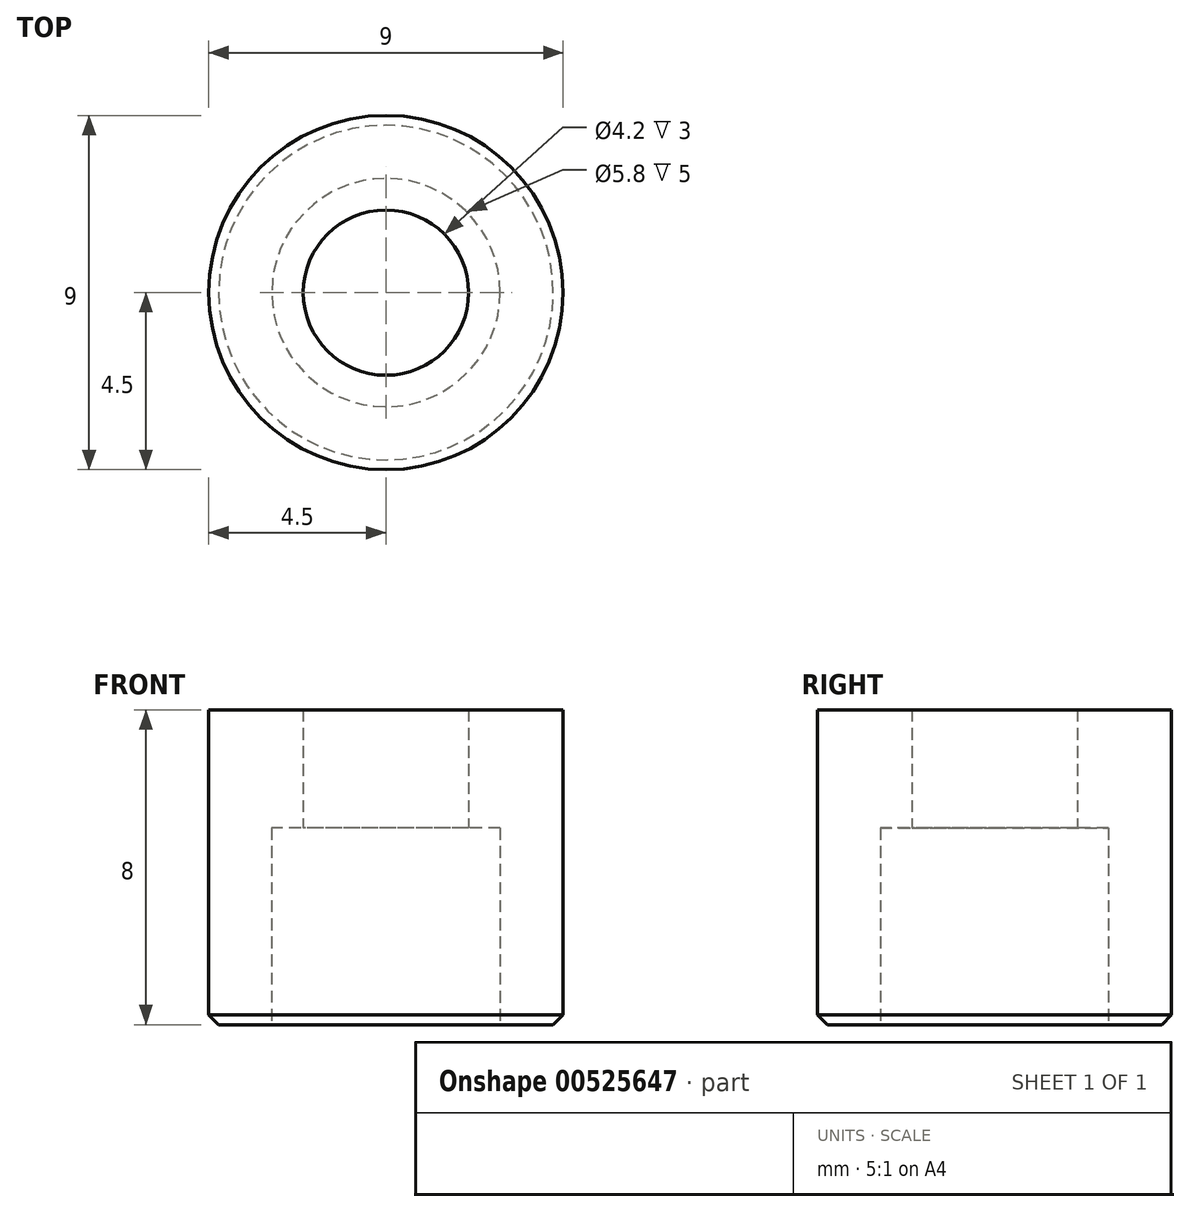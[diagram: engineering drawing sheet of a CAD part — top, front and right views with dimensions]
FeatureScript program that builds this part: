
annotation { "Feature Type Name" : "Feature", "Feature Type Description" : "" }
export const myFeature = defineFeature(function(context is Context, id is Id, definition is map)
    precondition{}
    {
        {
            var Q0;
            Q0=qCreatedBy(makeId("Top.planeOp"),FACE);
            var sketch = newSketch(context, id + "F0", { "sketchPlane" : qUnion([Q0])});
            skCircle(sketch, "E0", {"center": v(0, 0) * mm, "radius": 4.5 * mm});
            skCircle(sketch, "E1", {"center": v(0, 0) * mm, "radius": 2.9 * mm});
            skCircle(sketch, "E2", {"center": v(0, 0) * mm, "radius": 2.1 * mm});
            skSolve(sketch);
        }
        {
            var Q0;
            Q0=makeQuery(id+"F0.imprint","IMPRINT",FACE,{"disambiguationData":[TD([[makeQuery(id+"F0.imprint","IMPRINT",EDGE,{"derivedFrom":sQuery(id+"F0.wireOp",EDGE,"E2")}),1.0]])]});
            var Q1;
            Q1=makeQuery(id+"F0.imprint","IMPRINT",FACE,{"disambiguationData":[TD([[makeQuery(id+"F0.imprint","IMPRINT",EDGE,{"derivedFrom":sQuery(id+"F0.wireOp",EDGE,"E1")}),1.0]])]});
            var Q2;
            Q2=makeQuery(id+"F0.imprint","IMPRINT",FACE,{"disambiguationData":[TD([[makeQuery(id+"F0.imprint","IMPRINT",EDGE,{"derivedFrom":sQuery(id+"F0.wireOp",EDGE,"E0")}),1.0]])]});
            extrude(context, id + "F1", {"entities" : qUnion([Q0, Q1, Q2]), "depth" : 8 * mm, "offsetDistance" : 25 * mm});
        }
        {
            var Q0;
            Q0=makeQuery(id+"F0.imprint","IMPRINT",FACE,{"disambiguationData":[TD([[makeQuery(id+"F0.imprint","IMPRINT",EDGE,{"derivedFrom":sQuery(id+"F0.wireOp",EDGE,"E2")}),1.0]])]});
            extrude(context, id + "F2", {"entities" : qUnion([Q0]), "operationType" : NewBodyOperationType.REMOVE, "endBound" : BoundingType.THROUGH_ALL, "depth" : 25 * mm, "offsetDistance" : 25 * mm});
        }
        {
            var Q0;
            Q0=makeQuery(id+"F0.imprint","IMPRINT",FACE,{"disambiguationData":[TD([[makeQuery(id+"F0.imprint","IMPRINT",EDGE,{"derivedFrom":sQuery(id+"F0.wireOp",EDGE,"E1")}),1.0]])]});
            extrude(context, id + "F3", {"entities" : qUnion([Q0]), "operationType" : NewBodyOperationType.REMOVE, "depth" : 5 * mm, "offsetDistance" : 25 * mm});
        }
        {
            var Q0;
            Q0=makeQuery(id+"F3.boolean.opBoolean","COPY",EDGE,{"derivedFrom":makeQuery(id+"F3.opExtrude","CAP_EDGE",EDGE,{"disambiguationData":[OSD([sQuery(id+"F0.wireOp",EDGE,"E2")])],"isStart":false})});
            var Q1;
            Q1=makeQuery(id+"F3.boolean.opBoolean","COPY",EDGE,{"derivedFrom":makeQuery(id+"F3.opExtrude","CAP_EDGE",EDGE,{"disambiguationData":[OSD([sQuery(id+"F0.wireOp",EDGE,"E1")])],"isStart":true})});
            var Q2;
            Q2=makeQuery(id+"F1.opExtrude","CAP_EDGE",EDGE,{"disambiguationData":[OSD([sQuery(id+"F0.wireOp",EDGE,"E0")])],"isStart":true});
            chamfer(context, id + "F4", {"entities" : qUnion([Q0, Q1, Q2]), "width" : 0.25 * mm, "tangentPropagation" : true});
        }
    });
